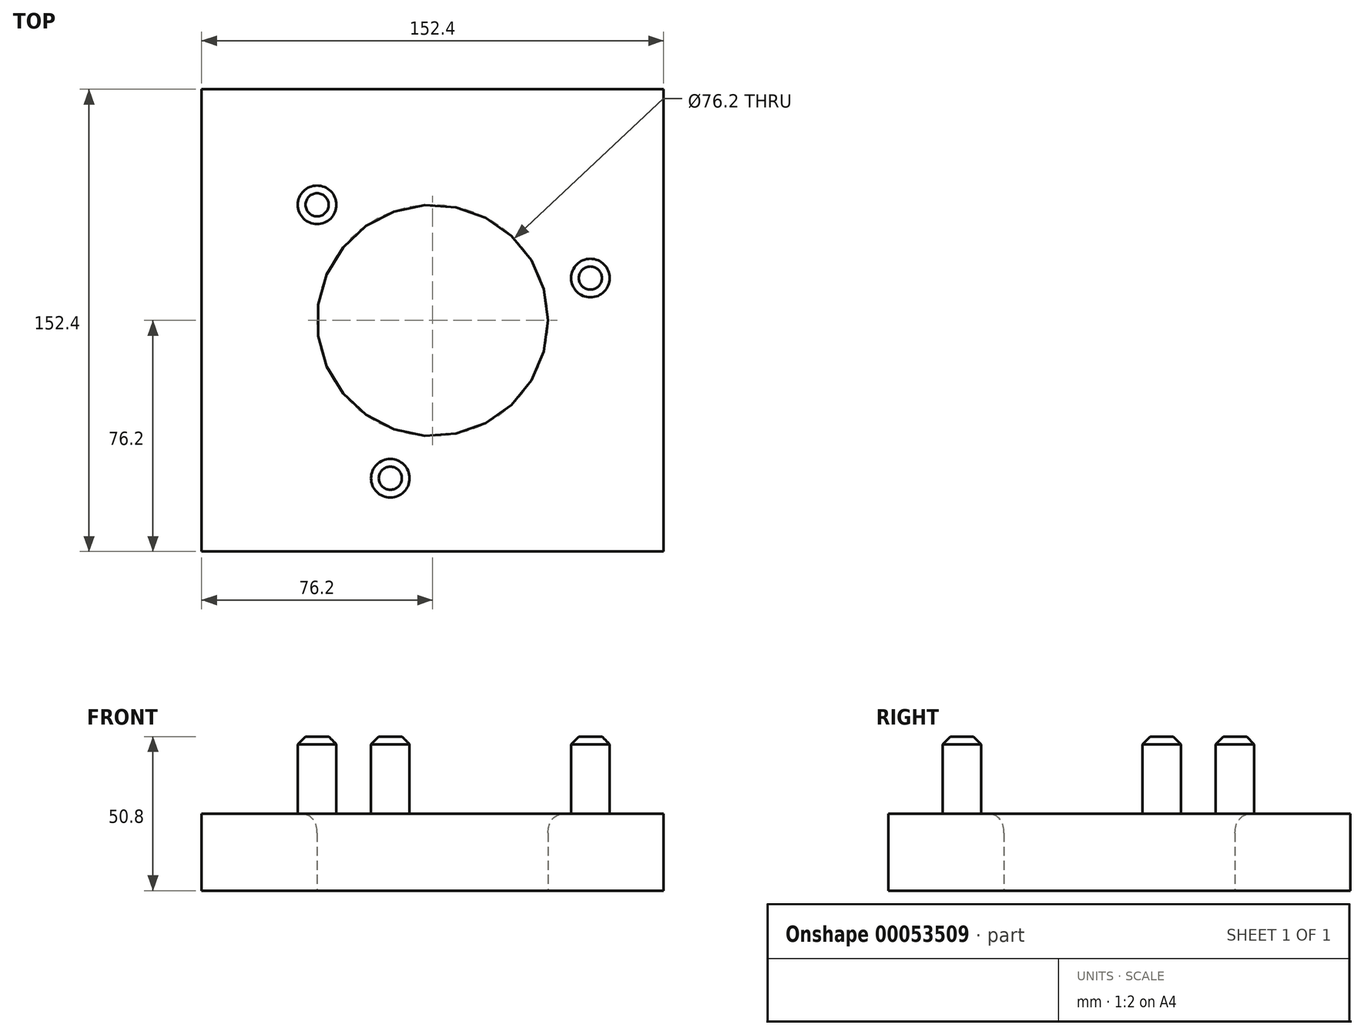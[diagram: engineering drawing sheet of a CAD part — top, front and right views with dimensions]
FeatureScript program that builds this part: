
annotation { "Feature Type Name" : "Feature", "Feature Type Description" : "" }
export const myFeature = defineFeature(function(context is Context, id is Id, definition is map)
    precondition{}
    {
        {
            var Q0;
            Q0=qCreatedBy(makeId("Top.planeOp"),FACE);
            var sketch = newSketch(context, id + "F0", { "sketchPlane" : qUnion([Q0])});
            skLineSegment(sketch, "E0", {"start": v(76.2, 76.2) * mm, "end": v(76.2, -76.2) * mm});
            skLineSegment(sketch, "E1", {"start": v(76.2, -76.2) * mm, "end": v(-76.2, -76.2) * mm});
            skLineSegment(sketch, "E2", {"start": v(-76.2, -76.2) * mm, "end": v(-76.2, 76.2) * mm});
            skCircle(sketch, "E3", {"center": v(0, 0) * mm, "radius": 38.1 * mm});
            skLineSegment(sketch, "E4", {"start": v(-76.2, 76.2) * mm, "end": v(76.2, 76.2) * mm});
            skSolve(sketch);
        }
        {
            var Q0;
            Q0=makeQuery(id+"F0.imprint","IMPRINT",FACE,{"disambiguationData":[TD([[makeQuery(id+"F0.imprint","IMPRINT",EDGE,{"derivedFrom":sQuery(id+"F0.wireOp",EDGE,"E0")}),-1.0]])]});
            extrude(context, id + "F1", {"entities" : qUnion([Q0]), "depth" : 25.4 * mm});
        }
        {
            var Q0;
            Q0=makeQuery(id+"F1.opExtrude","CAP_FACE",FACE,{"disambiguationData":[OSD([sQuery(id+"F0.wireOp",EDGE,"E0"),sQuery(id+"F0.wireOp",EDGE,"E1"),sQuery(id+"F0.wireOp",EDGE,"E2"),sQuery(id+"F0.wireOp",EDGE,"E3"),sQuery(id+"F0.wireOp",EDGE,"E4")])],"isStart":false});
            var sketch = newSketch(context, id + "F2", { "sketchPlane" : qUnion([Q0])});
            skCircle(sketch, "E5", {"center": v(-38.1, 38.1) * mm, "radius": 6.35 * mm});
            skCircle(sketch, "E6.1.0", {"center": v(52.05, 13.95) * mm, "radius": 6.35 * mm});
            skCircle(sketch, "E6.2.0", {"center": v(-13.95, -52.05) * mm, "radius": 6.35 * mm});
            skPoint(sketch, "E6.center", {"position": v(0, 0) * mm});
            skSolve(sketch);
        }
        {
            var Q0;
            Q0=makeQuery(id+"F2.imprint","IMPRINT",FACE,{"disambiguationData":[TD([[makeQuery(id+"F2.imprint","IMPRINT",EDGE,{"derivedFrom":sQuery(id+"F2.wireOp",EDGE,"E5")}),1.0]])]});
            var Q1;
            Q1=makeQuery(id+"F2.imprint","IMPRINT",FACE,{"disambiguationData":[TD([[makeQuery(id+"F2.imprint","IMPRINT",EDGE,{"derivedFrom":sQuery(id+"F2.wireOp",EDGE,"E6.2.0")}),1.0]])]});
            var Q2;
            Q2=makeQuery(id+"F2.imprint","IMPRINT",FACE,{"disambiguationData":[TD([[makeQuery(id+"F2.imprint","IMPRINT",EDGE,{"derivedFrom":sQuery(id+"F2.wireOp",EDGE,"E6.1.0")}),1.0]])]});
            extrude(context, id + "F3", {"entities" : qUnion([Q0, Q1, Q2]), "operationType" : NewBodyOperationType.ADD, "depth" : 25.4 * mm, "hasDraft" : true, "draftAngle" : 0 * degree});
        }
        {
            var Q0;
            Q0=makeQuery(id+"F1.opExtrude","CAP_EDGE",EDGE,{"disambiguationData":[OSD([sQuery(id+"F0.wireOp",EDGE,"E3")])],"isStart":false});
            fillet(context, id + "F4", {"entities" : qUnion([Q0]), "radius" : 6.35 * mm, "tangentPropagation" : true, "rho" : 0.5, "crossSection" : FilletCrossSection.CONIC, "allowEdgeOverflow" : false});
        }
        {
            var Q0;
            Q0=makeQuery(id+"F3.opExtrude","CAP_EDGE",EDGE,{"disambiguationData":[OSD([sQuery(id+"F2.wireOp",EDGE,"E5")])],"isStart":false});
            var Q1;
            Q1=makeQuery(id+"F3.opExtrude","CAP_EDGE",EDGE,{"disambiguationData":[OSD([sQuery(id+"F2.wireOp",EDGE,"E6.2.0")])],"isStart":false});
            var Q2;
            Q2=makeQuery(id+"F3.opExtrude","CAP_EDGE",EDGE,{"disambiguationData":[OSD([sQuery(id+"F2.wireOp",EDGE,"E6.1.0")])],"isStart":false});
            chamfer(context, id + "F5", {"entities" : qUnion([Q0, Q1, Q2]), "width" : 2.54 * mm, "tangentPropagation" : true});
        }
    });
